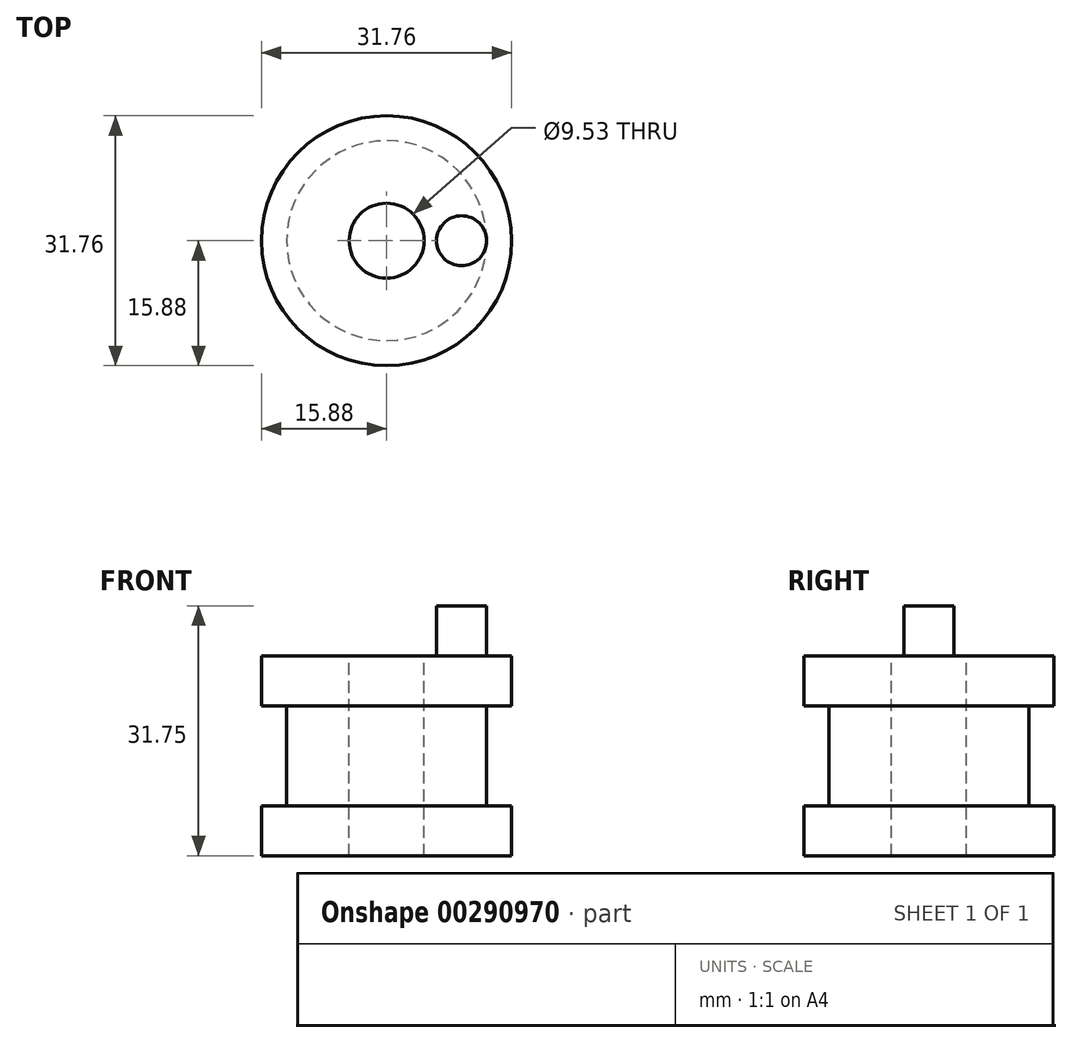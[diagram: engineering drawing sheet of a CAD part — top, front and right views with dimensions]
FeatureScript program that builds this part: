
annotation { "Feature Type Name" : "Feature", "Feature Type Description" : "" }
export const myFeature = defineFeature(function(context is Context, id is Id, definition is map)
    precondition{}
    {
        {
            var Q0;
            Q0=qCreatedBy(makeId("Front.planeOp"),FACE);
            var sketch = newSketch(context, id + "F0", { "sketchPlane" : qUnion([Q0])});
            skLineSegment(sketch, "E0.bottom", {"start": v(-12.7, 6.35) * mm, "end": v(12.7, 6.35) * mm});
            skLineSegment(sketch, "E0.top", {"start": v(-12.7, -6.35) * mm, "end": v(12.7, -6.35) * mm});
            skLineSegment(sketch, "E0.left", {"start": v(-12.7, 6.35) * mm, "end": v(-12.7, -6.35) * mm});
            skLineSegment(sketch, "E0.right", {"start": v(12.7, 6.35) * mm, "end": v(12.7, -6.35) * mm});
            skPoint(sketch, "E0.middle", {"position": v(0, 0) * mm});
            skLineSegment(sketch, "E1.bottom", {"start": v(-15.88, 12.7) * mm, "end": v(15.87, 12.7) * mm});
            skLineSegment(sketch, "E1.top", {"start": v(-15.88, 6.35) * mm, "end": v(15.87, 6.35) * mm});
            skLineSegment(sketch, "E1.left", {"start": v(-15.88, 12.7) * mm, "end": v(-15.88, 6.35) * mm});
            skLineSegment(sketch, "E1.right", {"start": v(15.87, 12.7) * mm, "end": v(15.87, 6.35) * mm});
            skPoint(sketch, "E1.middle", {"position": v(0, 9.53) * mm});
            skLineSegment(sketch, "E2.bottom", {"start": v(-15.88, -12.7) * mm, "end": v(15.88, -12.7) * mm});
            skLineSegment(sketch, "E2.top", {"start": v(-15.88, -6.35) * mm, "end": v(15.88, -6.35) * mm});
            skLineSegment(sketch, "E2.left", {"start": v(-15.88, -12.7) * mm, "end": v(-15.88, -6.35) * mm});
            skLineSegment(sketch, "E2.right", {"start": v(15.88, -12.7) * mm, "end": v(15.88, -6.35) * mm});
            skPoint(sketch, "E2.middle", {"position": v(0, -9.53) * mm});
            skLineSegment(sketch, "E3", {"start": v(0, 12.7) * mm, "end": v(0, -12.7) * mm});
            skLineSegment(sketch, "E4", {"start": v(4.76, 12.7) * mm, "end": v(4.76, -12.7) * mm});
            skSolve(sketch);
        }
        {
            var Q0;
            {var subQ0=sQuery(id+"F0.wireOp",EDGE,"E1.right");Q0=makeQuery(id+"F0.imprint","IMPRINT",FACE,{"disambiguationData":[TD([[makeQuery(id+"F0.imprint","IMPRINT",EDGE,{"derivedFrom":subQ0}),-1.0]])]});}
            var Q1;
            {var subQ0=sQuery(id+"F0.wireOp",EDGE,"E0.right");Q1=makeQuery(id+"F0.imprint","IMPRINT",FACE,{"disambiguationData":[TD([[makeQuery(id+"F0.imprint","IMPRINT",EDGE,{"derivedFrom":subQ0}),-1.0]])]});}
            var Q2;
            {var subQ0=sQuery(id+"F0.wireOp",EDGE,"E2.right");Q2=makeQuery(id+"F0.imprint","IMPRINT",FACE,{"disambiguationData":[TD([[makeQuery(id+"F0.imprint","IMPRINT",EDGE,{"derivedFrom":subQ0}),1.0]])]});}
            var Q3;
            Q3=sQuery(id+"F0.wireOp",EDGE,"E3");
            revolve(context, id + "F1", {"entities" : qUnion([Q0, Q1, Q2]), "axis" : qUnion([Q3]), "revolveType" : RevolveType.FULL});
        }
        {
            var Q0;
            Q0=makeQuery(id+"F1.opRevolve","SWEPT_FACE",FACE,{"disambiguationData":[OSD([sQuery(id+"F0.wireOp",EDGE,"E1.bottom")])]});
            var sketch = newSketch(context, id + "F2", { "sketchPlane" : qUnion([Q0])});
            skCircle(sketch, "E5", {"center": v(9.53, 0) * mm, "radius": 3.18 * mm});
            skSolve(sketch);
        }
        {
            var Q0;
            Q0=makeQuery(id+"F2.imprint","IMPRINT",FACE,{"disambiguationData":[TD([[makeQuery(id+"F2.imprint","IMPRINT",EDGE,{"derivedFrom":sQuery(id+"F2.wireOp",EDGE,"E5")}),1.0]])]});
            extrude(context, id + "F3", {"entities" : qUnion([Q0]), "operationType" : NewBodyOperationType.ADD, "depth" : 6.35 * mm});
        }
    });
